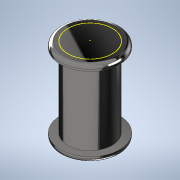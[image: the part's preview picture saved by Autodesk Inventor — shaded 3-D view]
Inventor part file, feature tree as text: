
AUTODESK INVENTOR PART (.ipt)
format: ipt  version: 2020.5 (Build 245400000, 400)  size: 141,824 bytes
history: native  units: mm
features: sketch x2, revolve x1, fillet x1, mirror x1
ambient origin geometry x8: Origin, YZ Plane, XZ Plane, XY Plane, X Axis, Y Axis, Z Axis, Center Point
bodies: Solid4 (feature_tree)
feature tree (5):
  revolve  "Revolution2"  [1 undecoded]
  fillet  "Fillet1"  Radius=4.0mm
  mirror  "Mirror1"
  sketch  "Boceto5"  dims[d36=0.75mm d37=90.0deg d41=0.5mm]
  sketch  "Sketch4"  dims[d32=3.0mm d33=5.0mm d35=4.0mm]
note: 1 required parameter value undecoded (feature->parameter linkage not recoverable at this tier; creation-order binding heuristic only, values carry confidence <= 0.55)
